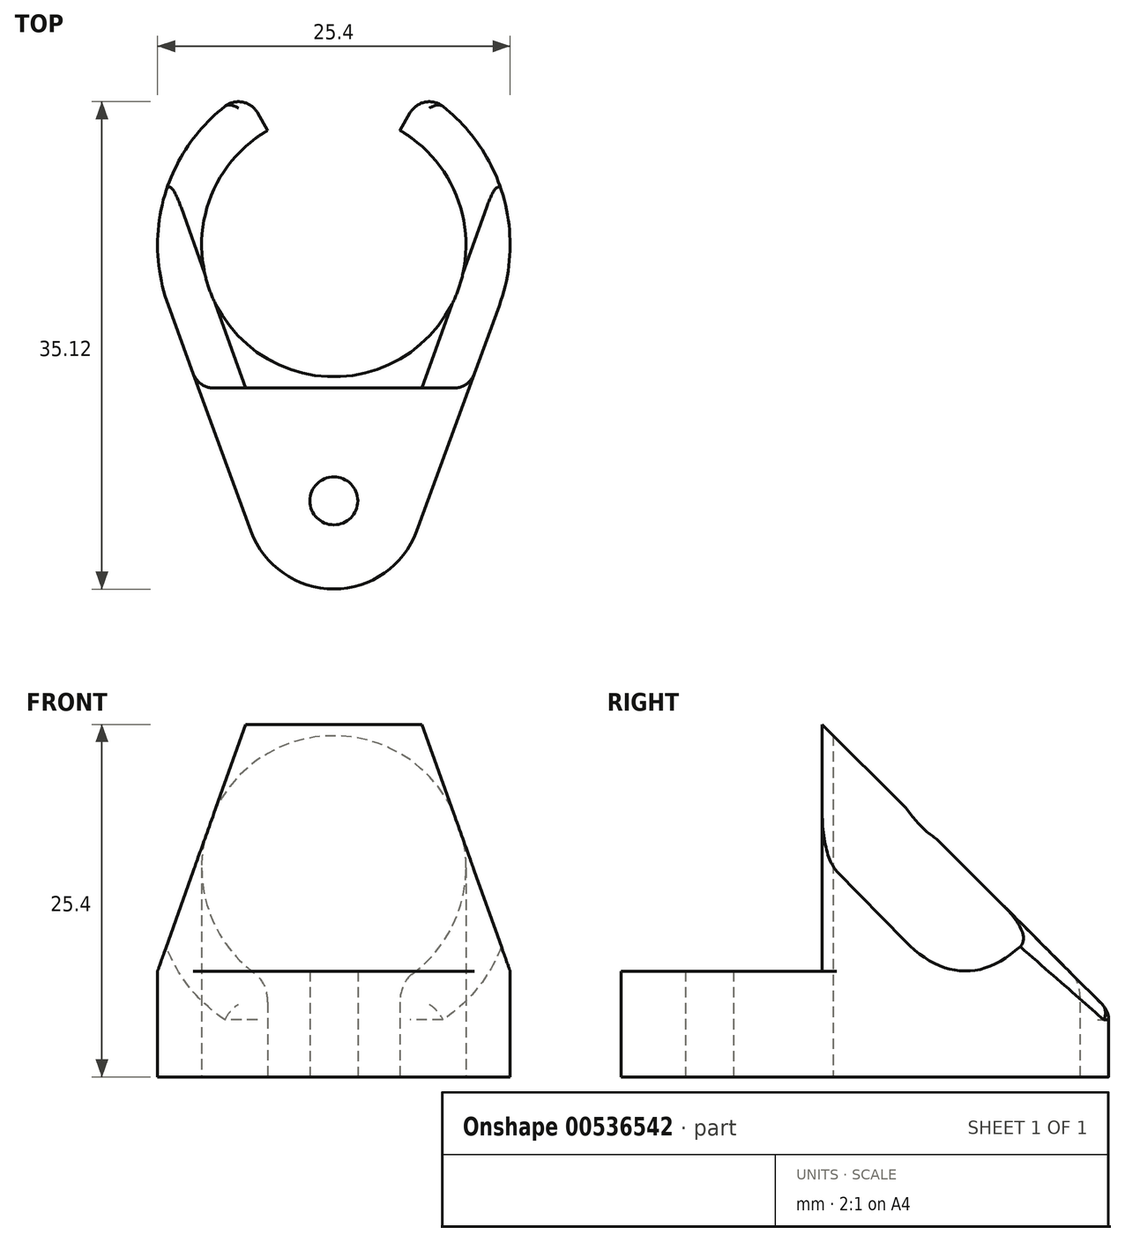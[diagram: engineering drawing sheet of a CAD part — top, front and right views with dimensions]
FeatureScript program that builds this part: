
annotation { "Feature Type Name" : "Feature", "Feature Type Description" : "" }
export const myFeature = defineFeature(function(context is Context, id is Id, definition is map)
    precondition{}
    {
        {
            var Q0;
            Q0=qCreatedBy(makeId("Top.planeOp"),FACE);
            var sketch = newSketch(context, id + "F0", { "sketchPlane" : qUnion([Q0])});
            skLineSegment(sketch, "E0", {"start": v(-5.96, -20.63) * mm, "end": v(-11.92, -4.37) * mm});
            skArc(sketch, "E1", {"start": v(-11.92, -4.37) * mm, "mid": v(0, 12.7) * mm, "end": v(11.92, -4.37) * mm, "construction": true});
            skLineSegment(sketch, "E2", {"start": v(11.92, -4.37) * mm, "end": v(5.96, -20.63) * mm});
            skLineSegment(sketch, "E3", {"start": v(-5.96, -20.63) * mm, "end": v(5.96, -20.63) * mm, "construction": true});
            skLineSegment(sketch, "E4", {"start": v(0, 0) * mm, "end": v(0, -20.63) * mm, "construction": true});
            skArc(sketch, "E5", {"start": v(5.96, -20.63) * mm, "mid": v(0, -24.8) * mm, "end": v(-5.96, -20.63) * mm});
            skLineSegment(sketch, "E6", {"start": v(-11.43, -10.32) * mm, "end": v(14.82, -10.32) * mm, "construction": true});
            skCircle(sketch, "E7", {"center": v(0, 0) * mm, "radius": 9.53 * mm, "construction": true});
            skLineSegment(sketch, "E8", {"start": v(0, 0) * mm, "end": v(-11.01, 19.08) * mm, "construction": true});
            skLineSegment(sketch, "E9", {"start": v(0, 0) * mm, "end": v(11.01, 19.08) * mm, "construction": true});
            skArc(sketch, "E10", {"start": v(-4.76, 8.25) * mm, "mid": v(0, -9.53) * mm, "end": v(4.76, 8.25) * mm});
            skArc(sketch, "E11", {"start": v(-6.35, 11) * mm, "mid": v(-11.94, 4.33) * mm, "end": v(-11.92, -4.37) * mm});
            skArc(sketch, "E12", {"start": v(11.92, -4.37) * mm, "mid": v(11.94, 4.33) * mm, "end": v(6.35, 11) * mm});
            skLineSegment(sketch, "E13", {"start": v(-6.35, 11) * mm, "end": v(-4.76, 8.25) * mm});
            skLineSegment(sketch, "E14", {"start": v(4.76, 8.25) * mm, "end": v(6.35, 11) * mm});
            skSolve(sketch);
        }
        {
            var Q0;
            Q0 = qSketchRegion(id + "F0", true);
            extrude(context, id + "F1", {"entities" : qUnion([Q0]), "depth" : 25.4 * mm, "offsetDistance" : 25.4 * mm});
        }
        {
            var Q0;
            Q0=qCreatedBy(makeId("Right.planeOp"),FACE);
            var sketch = newSketch(context, id + "F2", { "sketchPlane" : qUnion([Q0])});
            skPoint(sketch, "E15", {"position": v(-18.45, 0) * mm});
            skLineSegment(sketch, "E16", {"start": v(-10.32, 7.62) * mm, "end": v(-10.32, 25.4) * mm});
            skLineSegment(sketch, "E17", {"start": v(-10.32, 7.62) * mm, "end": v(-10.32, 0) * mm, "construction": true});
            skLineSegment(sketch, "E18", {"start": v(-10.32, 7.62) * mm, "end": v(-35.72, 7.62) * mm});
            skLineSegment(sketch, "E19", {"start": v(-35.72, 7.62) * mm, "end": v(-35.72, 48.47) * mm});
            skLineSegment(sketch, "E20", {"start": v(-10.32, 25.4) * mm, "end": v(26.2, -11.12) * mm});
            skLineSegment(sketch, "E21", {"start": v(26.2, -11.12) * mm, "end": v(26.2, 48.47) * mm});
            skLineSegment(sketch, "E22", {"start": v(26.2, 48.47) * mm, "end": v(-35.72, 48.47) * mm});
            skSolve(sketch);
        }
        {
            var Q0;
            Q0 = qSketchRegion(id + "F2", true);
            extrude(context, id + "F3", {"entities" : qUnion([Q0]), "operationType" : NewBodyOperationType.REMOVE, "endBound" : BoundingType.SYMMETRIC, "oppositeDirection" : true, "depth" : 50.8 * mm, "offsetDistance" : 25.4 * mm});
        }
        {
            var Q0;
            Q0=sQuery(id+"F0.wireOp",VERTEX,"E5.center");
            var Q1;
            Q1=makeQuery(id+"F1.opExtrude","SWEPT_BODY",BODY,{"disambiguationData":[OSD([sQuery(id+"F0.wireOp",EDGE,"E0"),sQuery(id+"F0.wireOp",EDGE,"E2"),sQuery(id+"F0.wireOp",EDGE,"E5"),sQuery(id+"F0.wireOp",EDGE,"E10"),sQuery(id+"F0.wireOp",EDGE,"E11"),sQuery(id+"F0.wireOp",EDGE,"E12"),sQuery(id+"F0.wireOp",EDGE,"E13"),sQuery(id+"F0.wireOp",EDGE,"E14")])]});
            hole(context, id + "F4", {"style" : HoleStyle.SIMPLE, "endStyle" : HoleEndStyle.THROUGH, "oppositeDirection" : true, "standardTappedOrClearance" : lookupTablePath({ "standard" : "ANSI", "engagement" : "75%", "pitch" : "32 tpi", "size" : "#8", "type" : "Tapped" }), "standardBlindInLast" : lookupTablePath({ "standard" : "ANSI", "engagement" : "75%", "pitch" : "32 tpi", "size" : "#8", "type" : "Tapped" }), "holeDiameter" : 3.45 * mm, "majorDiameter" : 4.17 * mm, "showTappedDepth" : true, "isTappedThrough" : true, "tappedDepth" : 15.88 * mm, "tapClearance" : 3, "startFromSketch" : true, "locations" : qUnion([Q0]), "scope" : qUnion([Q1])});
        }
        {
            var Q0;
            Q0=qCreatedBy(makeId("Front.planeOp"),FACE);
            var sketch = newSketch(context, id + "F5", { "sketchPlane" : qUnion([Q0])});
            skLineSegment(sketch, "E23", {"start": v(12.7, 7.62) * mm, "end": v(-12.7, 7.62) * mm, "construction": true});
            skLineSegment(sketch, "E24", {"start": v(0, 7.62) * mm, "end": v(0, 34.35) * mm, "construction": true});
            skLineSegment(sketch, "E25", {"start": v(15.42, 0) * mm, "end": v(6.35, 25.4) * mm});
            skLineSegment(sketch, "E26", {"start": v(6.35, 25.4) * mm, "end": v(-6.35, 25.4) * mm});
            skLineSegment(sketch, "E27", {"start": v(-6.35, 25.4) * mm, "end": v(-15.42, 0) * mm});
            skLineSegment(sketch, "E28", {"start": v(-15.42, 0) * mm, "end": v(15.42, 0) * mm});
            skLineSegment(sketch, "E29", {"start": v(0, 7.62) * mm, "end": v(0, 0) * mm, "construction": true});
            skSolve(sketch);
        }
        {
            var Q0;
            Q0 = qSketchRegion(id + "F5", true);
            extrude(context, id + "F6", {"entities" : qUnion([Q0]), "operationType" : NewBodyOperationType.INTERSECT, "endBound" : BoundingType.SYMMETRIC, "depth" : 50.8 * mm, "offsetDistance" : 25.4 * mm});
        }
        {
            var Q0;
            Q0=makeQuery(id+"F3.boolean.opBoolean","INTERSECT",EDGE,{"derivedFrom":[makeQuery(id+"F1.opExtrude","SWEPT_FACE",FACE,{"disambiguationData":[OSD([sQuery(id+"F0.wireOp",EDGE,"E11")])]}),makeQuery(id+"F3.opExtrude","SWEPT_FACE",FACE,{"disambiguationData":[OSD([sQuery(id+"F2.wireOp",EDGE,"E20")])]})]});
            var Q1;
            Q1=makeQuery(id+"F3.boolean.opBoolean","INTERSECT",EDGE,{"derivedFrom":[makeQuery(id+"F1.opExtrude","SWEPT_FACE",FACE,{"disambiguationData":[OSD([sQuery(id+"F0.wireOp",EDGE,"E12")])]}),makeQuery(id+"F3.opExtrude","SWEPT_FACE",FACE,{"disambiguationData":[OSD([sQuery(id+"F2.wireOp",EDGE,"E20")])]})]});
            var Q2;
            Q2=makeQuery(id+"F3.boolean.opBoolean","INTERSECT",EDGE,{"derivedFrom":[makeQuery(id+"F1.opExtrude","SWEPT_FACE",FACE,{"disambiguationData":[OSD([sQuery(id+"F0.wireOp",EDGE,"E14")])]}),makeQuery(id+"F3.opExtrude","SWEPT_FACE",FACE,{"disambiguationData":[OSD([sQuery(id+"F2.wireOp",EDGE,"E20")])]})]});
            var Q3;
            Q3=makeQuery(id+"F3.boolean.opBoolean","INTERSECT",EDGE,{"derivedFrom":[makeQuery(id+"F1.opExtrude","SWEPT_FACE",FACE,{"disambiguationData":[OSD([sQuery(id+"F0.wireOp",EDGE,"E13")])]}),makeQuery(id+"F3.opExtrude","SWEPT_FACE",FACE,{"disambiguationData":[OSD([sQuery(id+"F2.wireOp",EDGE,"E20")])]})]});
            var Q4;
            Q4=makeQuery(id+"F1.opExtrude","SWEPT_EDGE",EDGE,{"disambiguationData":[OSD([sQuery(id+"F0.wireOp",EDGE,"E12"),sQuery(id+"F0.wireOp",EDGE,"E14")])]});
            var Q5;
            Q5=makeQuery(id+"F1.opExtrude","SWEPT_EDGE",EDGE,{"disambiguationData":[OSD([sQuery(id+"F0.wireOp",EDGE,"E11"),sQuery(id+"F0.wireOp",EDGE,"E13")])]});
            var Q6;
            Q6=makeQuery(id+"F6.boolean.opBoolean","INTERSECT",EDGE,{"derivedFrom":[makeQuery(id+"F1.opExtrude","SWEPT_FACE",FACE,{"disambiguationData":[OSD([sQuery(id+"F0.wireOp",EDGE,"E12")])]}),makeQuery(id+"F6.boolean.toolComplement.opBoolean","COPY",FACE,{"derivedFrom":makeQuery(id+"F6.opExtrude","SWEPT_FACE",FACE,{"disambiguationData":[OSD([sQuery(id+"F5.wireOp",EDGE,"E25")])]})})]});
            var Q7;
            Q7=makeQuery(id+"F6.boolean.opBoolean","INTERSECT",EDGE,{"disambiguationData":[OD(1.0)],"derivedFrom":[makeQuery(id+"F3.boolean.opBoolean","COPY",FACE,{"derivedFrom":makeQuery(id+"F3.opExtrude","SWEPT_FACE",FACE,{"disambiguationData":[OSD([sQuery(id+"F2.wireOp",EDGE,"E20")])]})}),makeQuery(id+"F6.boolean.toolComplement.opBoolean","COPY",FACE,{"derivedFrom":makeQuery(id+"F6.opExtrude","SWEPT_FACE",FACE,{"disambiguationData":[OSD([sQuery(id+"F5.wireOp",EDGE,"E25")])]})})]});
            var Q8;
            Q8=makeQuery(id+"F6.boolean.opBoolean","INTERSECT",EDGE,{"derivedFrom":[makeQuery(id+"F1.opExtrude","SWEPT_FACE",FACE,{"disambiguationData":[OSD([sQuery(id+"F0.wireOp",EDGE,"E11")])]}),makeQuery(id+"F6.boolean.toolComplement.opBoolean","COPY",FACE,{"derivedFrom":makeQuery(id+"F6.opExtrude","SWEPT_FACE",FACE,{"disambiguationData":[OSD([sQuery(id+"F5.wireOp",EDGE,"E27")])]})})]});
            var Q9;
            Q9=makeQuery(id+"F6.boolean.opBoolean","INTERSECT",EDGE,{"disambiguationData":[OD(0.0)],"derivedFrom":[makeQuery(id+"F3.boolean.opBoolean","COPY",FACE,{"derivedFrom":makeQuery(id+"F3.opExtrude","SWEPT_FACE",FACE,{"disambiguationData":[OSD([sQuery(id+"F2.wireOp",EDGE,"E20")])]})}),makeQuery(id+"F6.boolean.toolComplement.opBoolean","COPY",FACE,{"derivedFrom":makeQuery(id+"F6.opExtrude","SWEPT_FACE",FACE,{"disambiguationData":[OSD([sQuery(id+"F5.wireOp",EDGE,"E27")])]})})]});
            var Q10;
            Q10=makeQuery(id+"F3.boolean.opBoolean","INTERSECT",EDGE,{"derivedFrom":[makeQuery(id+"F1.opExtrude","SWEPT_FACE",FACE,{"disambiguationData":[OSD([sQuery(id+"F0.wireOp",EDGE,"E0")])]}),makeQuery(id+"F3.opExtrude","SWEPT_FACE",FACE,{"disambiguationData":[OSD([sQuery(id+"F2.wireOp",EDGE,"E16")])]})]});
            var Q11;
            Q11=makeQuery(id+"F3.boolean.opBoolean","INTERSECT",EDGE,{"derivedFrom":[makeQuery(id+"F1.opExtrude","SWEPT_FACE",FACE,{"disambiguationData":[OSD([sQuery(id+"F0.wireOp",EDGE,"E2")])]}),makeQuery(id+"F3.opExtrude","SWEPT_FACE",FACE,{"disambiguationData":[OSD([sQuery(id+"F2.wireOp",EDGE,"E16")])]})]});
            var Q12;
            Q12=makeQuery(id+"F6.boolean.opBoolean","INTERSECT",EDGE,{"derivedFrom":[makeQuery(id+"F3.boolean.opBoolean","COPY",FACE,{"derivedFrom":makeQuery(id+"F3.opExtrude","SWEPT_FACE",FACE,{"disambiguationData":[OSD([sQuery(id+"F2.wireOp",EDGE,"E16")])]})}),makeQuery(id+"F6.boolean.toolComplement.opBoolean","COPY",FACE,{"derivedFrom":makeQuery(id+"F6.opExtrude","SWEPT_FACE",FACE,{"disambiguationData":[OSD([sQuery(id+"F5.wireOp",EDGE,"E25")])]})})]});
            var Q13;
            Q13=makeQuery(id+"F6.boolean.opBoolean","INTERSECT",EDGE,{"derivedFrom":[makeQuery(id+"F3.boolean.opBoolean","COPY",FACE,{"derivedFrom":makeQuery(id+"F3.opExtrude","SWEPT_FACE",FACE,{"disambiguationData":[OSD([sQuery(id+"F2.wireOp",EDGE,"E16")])]})}),makeQuery(id+"F6.boolean.toolComplement.opBoolean","COPY",FACE,{"derivedFrom":makeQuery(id+"F6.opExtrude","SWEPT_FACE",FACE,{"disambiguationData":[OSD([sQuery(id+"F5.wireOp",EDGE,"E27")])]})})]});
            fillet(context, id + "F7", {"entities" : qUnion([Q0, Q1, Q2, Q3, Q4, Q5, Q6, Q7, Q8, Q9, Q10, Q11, Q12, Q13]), "radius" : 1.59 * mm, "tangentPropagation" : true, "allowEdgeOverflow" : false});
        }
    });
